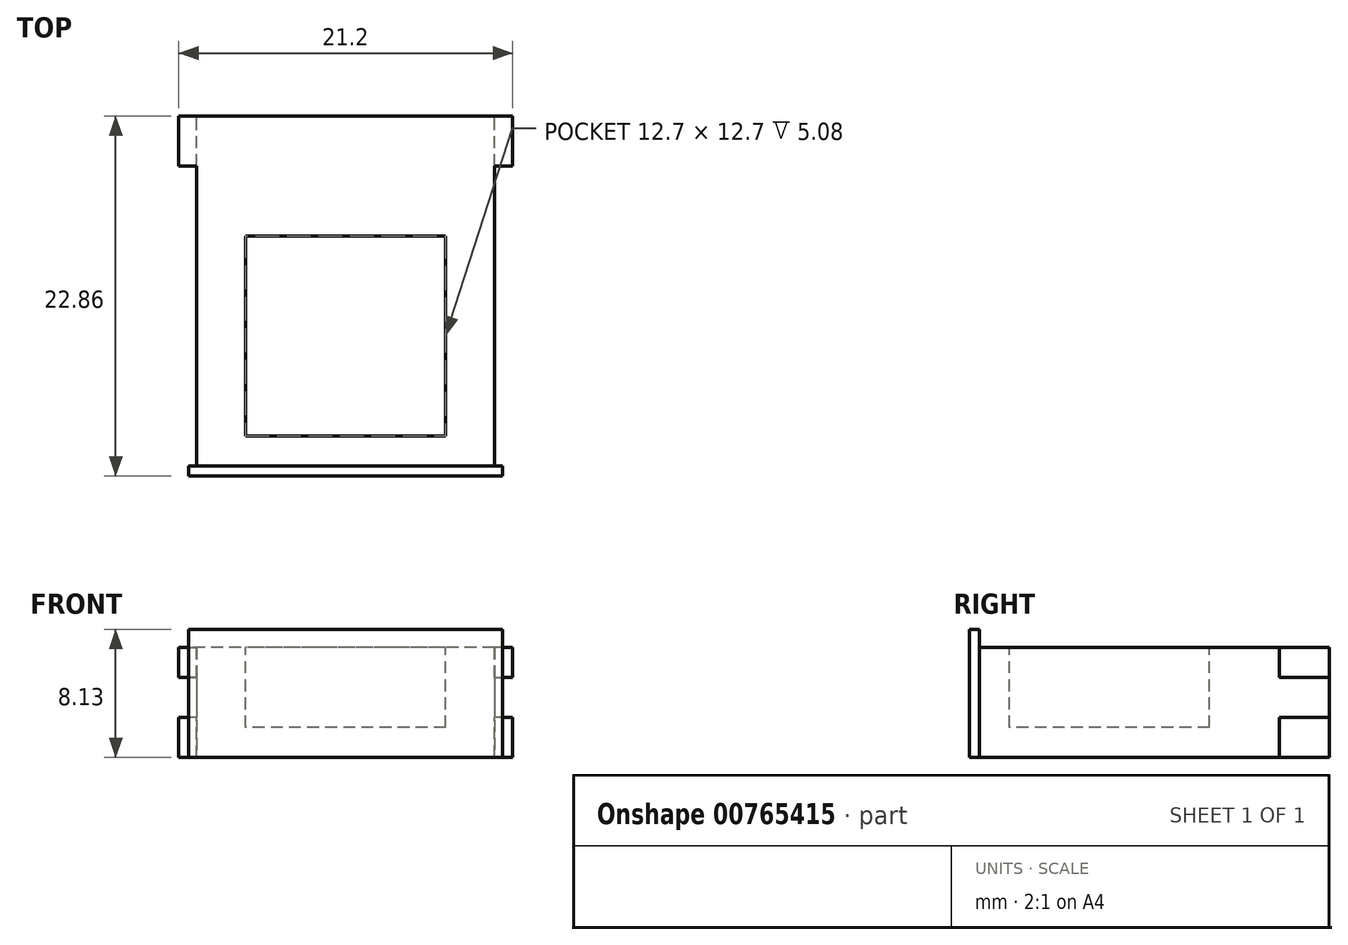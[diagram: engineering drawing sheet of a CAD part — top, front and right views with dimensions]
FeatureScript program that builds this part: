
annotation { "Feature Type Name" : "Feature", "Feature Type Description" : "" }
export const myFeature = defineFeature(function(context is Context, id is Id, definition is map)
    precondition{}
    {
        {
            var Q0;
            Q0=qCreatedBy(makeId("Front.planeOp"),FACE);
            var sketch = newSketch(context, id + "F0", { "sketchPlane" : qUnion([Q0])});
            skLineSegment(sketch, "E0.bottom", {"start": v(9.46, 3.18) * mm, "end": v(-9.46, 3.17) * mm});
            skLineSegment(sketch, "E0.top", {"start": v(9.46, -3.8) * mm, "end": v(-9.46, -3.81) * mm});
            skLineSegment(sketch, "E0.left", {"start": v(9.46, 3.18) * mm, "end": v(9.46, -3.8) * mm});
            skLineSegment(sketch, "E0.right", {"start": v(-9.46, 3.17) * mm, "end": v(-9.46, -3.81) * mm});
            skPoint(sketch, "E0.middle", {"position": v(0, 0) * mm});
            skSolve(sketch);
        }
        {
            var Q0;
            Q0=makeQuery(id+"F0.imprint","IMPRINT",FACE,{"disambiguationData":[TD([[makeQuery(id+"F0.imprint","IMPRINT",EDGE,{"derivedFrom":sQuery(id+"F0.wireOp",EDGE,"E0.bottom")}),1.0]])]});
            extrude(context, id + "F1", {"entities" : qUnion([Q0]), "depth" : 22.86 * mm, "offsetDistance" : 25.4 * mm});
        }
        {
            var Q0;
            Q0=makeQuery(id+"F1.opExtrude","CAP_FACE",FACE,{"disambiguationData":[OSD([sQuery(id+"F0.wireOp",EDGE,"E0.bottom"),sQuery(id+"F0.wireOp",EDGE,"E0.top"),sQuery(id+"F0.wireOp",EDGE,"E0.left"),sQuery(id+"F0.wireOp",EDGE,"E0.right")])],"isStart":false});
            var sketch = newSketch(context, id + "F2", { "sketchPlane" : qUnion([Q0])});
            skLineSegment(sketch, "E1.0", {"start": v(-9.97, 4.32) * mm, "end": v(-9.97, -3.81) * mm});
            skLineSegment(sketch, "E1.1", {"start": v(9.98, 4.32) * mm, "end": v(-9.97, 4.32) * mm});
            skLineSegment(sketch, "E1.2", {"start": v(9.98, 4.32) * mm, "end": v(9.98, -3.8) * mm});
            skLineSegment(sketch, "E1.3", {"start": v(9.98, -3.8) * mm, "end": v(-9.97, -3.81) * mm});
            skSolve(sketch);
        }
        {
            var Q0;
            Q0=makeQuery(id+"F2.imprint","IMPRINT",FACE,{"disambiguationData":[TD([[makeQuery(id+"F2.imprint","IMPRINT",EDGE,{"derivedFrom":sQuery(id+"F2.wireOp",EDGE,"E1.0")}),1.0]])]});
            extrude(context, id + "F3", {"entities" : qUnion([Q0]), "operationType" : NewBodyOperationType.ADD, "oppositeDirection" : true, "depth" : 0.64 * mm, "offsetDistance" : 25.4 * mm});
        }
        {
            var Q0;
            Q0=makeQuery(id+"F1.opExtrude","SWEPT_FACE",FACE,{"disambiguationData":[OSD([sQuery(id+"F0.wireOp",EDGE,"E0.bottom")])]});
            var sketch = newSketch(context, id + "F4", { "sketchPlane" : qUnion([Q0])});
            skPoint(sketch, "E2", {"position": v(0, -13.97) * mm});
            skLineSegment(sketch, "E3", {"start": v(-9.46, 0) * mm, "end": v(-10.6, 0) * mm});
            skLineSegment(sketch, "E4", {"start": v(-10.6, 0) * mm, "end": v(-10.6, -3.17) * mm});
            skLineSegment(sketch, "E5", {"start": v(-10.6, -3.17) * mm, "end": v(-9.46, -3.17) * mm});
            skLineSegment(sketch, "E6.MirrorCS", {"start": v(9.46, 0) * mm, "end": v(10.6, 0) * mm});
            skLineSegment(sketch, "E7.MirrorCS", {"start": v(10.6, 0) * mm, "end": v(10.6, -3.17) * mm});
            skLineSegment(sketch, "E8.MirrorCS", {"start": v(10.6, -3.17) * mm, "end": v(9.46, -3.17) * mm});
            skLineSegment(sketch, "E9.bottom", {"start": v(6.35, -7.62) * mm, "end": v(-6.35, -7.62) * mm});
            skLineSegment(sketch, "E9.top", {"start": v(6.35, -20.32) * mm, "end": v(-6.35, -20.32) * mm});
            skLineSegment(sketch, "E9.left", {"start": v(6.35, -7.62) * mm, "end": v(6.35, -20.32) * mm});
            skLineSegment(sketch, "E9.right", {"start": v(-6.35, -7.62) * mm, "end": v(-6.35, -20.32) * mm});
            skSolve(sketch);
        }
        {
            var Q0;
            Q0=makeQuery(id+"F4.imprint","IMPRINT",FACE,{"disambiguationData":[TD([[makeQuery(id+"F4.imprint","IMPRINT",EDGE,{"derivedFrom":sQuery(id+"F4.wireOp",EDGE,"aHxRyVL1-Kome-zMzx-eloK-K6PUuLpYeDD1")}),1.0]])]});
            var Q1;
            Q1=makeQuery(id+"F4.imprint","IMPRINT",FACE,{"disambiguationData":[TD([[makeQuery(id+"F4.imprint","IMPRINT",EDGE,{"derivedFrom":sQuery(id+"F4.wireOp",EDGE,"E9.bottom")}),1.0]])]});
            extrude(context, id + "F5", {"entities" : qUnion([Q0, Q1]), "operationType" : NewBodyOperationType.REMOVE, "oppositeDirection" : true, "depth" : 5.08 * mm, "offsetDistance" : 25.4 * mm});
        }
        {
            var Q0;
            {var subQ0=sQuery(id+"F4.wireOp",EDGE,"E3");Q0=makeQuery(id+"F4.imprint","IMPRINT",FACE,{"disambiguationData":[TD([[makeQuery(id+"F4.imprint","IMPRINT",EDGE,{"derivedFrom":subQ0}),1.0]])]});}
            var Q1;
            {var subQ0=sQuery(id+"F4.wireOp",EDGE,"E6.MirrorCS");Q1=makeQuery(id+"F4.imprint","IMPRINT",FACE,{"disambiguationData":[TD([[makeQuery(id+"F4.imprint","IMPRINT",EDGE,{"derivedFrom":subQ0}),-1.0]])]});}
            var Q2;
            {var subQ0=sQuery(id+"F2.wireOp",EDGE,"E1.3");Q2=makeQuery(id+"F3.boolean.opBoolean","MERGE",FACE,{"derivedFrom":[makeQuery(id+"F1.opExtrude","SWEPT_FACE",FACE,{"disambiguationData":[OSD([sQuery(id+"F0.wireOp",EDGE,"E0.top")])]}),makeQuery(id+"F3.opExtrude","SWEPT_FACE",FACE,{"disambiguationData":[OSD([subQ0]),TDD([makeQuery(id+"F2.imprint","IMPRINT",EDGE,{"disambiguationData":[TD([[makeQuery(id+"F2.imprint","INTERSECT",VERTEX,{"derivedFrom":[makeQuery(id+"F1.opExtrude","CAP_EDGE",EDGE,{"disambiguationData":[OSD([sQuery(id+"F0.wireOp",EDGE,"E0.left")])],"isStart":false}),subQ0]}),1.0]])],"derivedFrom":subQ0})])]}),makeQuery(id+"F3.opExtrude","SWEPT_FACE",FACE,{"disambiguationData":[OSD([subQ0]),TDD([makeQuery(id+"F2.imprint","IMPRINT",EDGE,{"disambiguationData":[TD([[makeQuery(id+"F2.imprint","INTERSECT",VERTEX,{"derivedFrom":[makeQuery(id+"F1.opExtrude","CAP_EDGE",EDGE,{"disambiguationData":[OSD([sQuery(id+"F0.wireOp",EDGE,"E0.right")])],"isStart":false}),subQ0]}),-1.0]])],"derivedFrom":subQ0})])]})]});}
            extrude(context, id + "F6", {"entities" : qUnion([Q0, Q1]), "operationType" : NewBodyOperationType.ADD, "endBound" : BoundingType.UP_TO_SURFACE, "oppositeDirection" : true, "depth" : 25.4 * mm, "endBoundEntityFace" : qUnion([Q2]), "offsetDistance" : 25.4 * mm});
        }
        {
            var Q0;
            Q0=makeQuery(id+"F0.imprint","IMPRINT",FACE,{"disambiguationData":[TD([[makeQuery(id+"F0.imprint","IMPRINT",EDGE,{"derivedFrom":sQuery(id+"F0.wireOp",EDGE,"E0.bottom")}),1.0]])]});
            var sketch = newSketch(context, id + "F7", { "sketchPlane" : qUnion([Q0])});
            skLineSegment(sketch, "E10", {"start": v(9.46, 1.27) * mm, "end": v(10.6, 1.27) * mm});
            skLineSegment(sketch, "E11", {"start": v(10.6, 1.27) * mm, "end": v(10.6, -1.27) * mm});
            skLineSegment(sketch, "E12", {"start": v(10.6, -1.27) * mm, "end": v(9.46, -1.27) * mm});
            skLineSegment(sketch, "E13.MirrorCS", {"start": v(-9.46, 1.27) * mm, "end": v(-10.6, 1.27) * mm});
            skLineSegment(sketch, "E14.MirrorCS", {"start": v(-10.6, 1.27) * mm, "end": v(-10.6, -1.27) * mm});
            skLineSegment(sketch, "E15.MirrorCS", {"start": v(-10.6, -1.27) * mm, "end": v(-9.46, -1.27) * mm});
            skLineSegment(sketch, "E16", {"start": v(9.46, 1.27) * mm, "end": v(9.46, -1.27) * mm});
            skLineSegment(sketch, "E17.MirrorCS", {"start": v(-9.46, 1.27) * mm, "end": v(-9.46, -1.27) * mm});
            skSolve(sketch);
        }
        {
            var Q0;
            Q0=makeQuery(id+"F7.imprint","IMPRINT",FACE,{"disambiguationData":[TD([[makeQuery(id+"F7.imprint","IMPRINT",EDGE,{"derivedFrom":sQuery(id+"F7.wireOp",EDGE,"E10")}),-1.0]])]});
            var Q1;
            Q1=makeQuery(id+"F7.imprint","IMPRINT",FACE,{"disambiguationData":[TD([[makeQuery(id+"F7.imprint","IMPRINT",EDGE,{"derivedFrom":sQuery(id+"F7.wireOp",EDGE,"E13.MirrorCS")}),1.0]])]});
            extrude(context, id + "F8", {"entities" : qUnion([Q0, Q1]), "operationType" : NewBodyOperationType.REMOVE, "depth" : 12.7 * mm, "offsetDistance" : 25.4 * mm});
        }
    });
